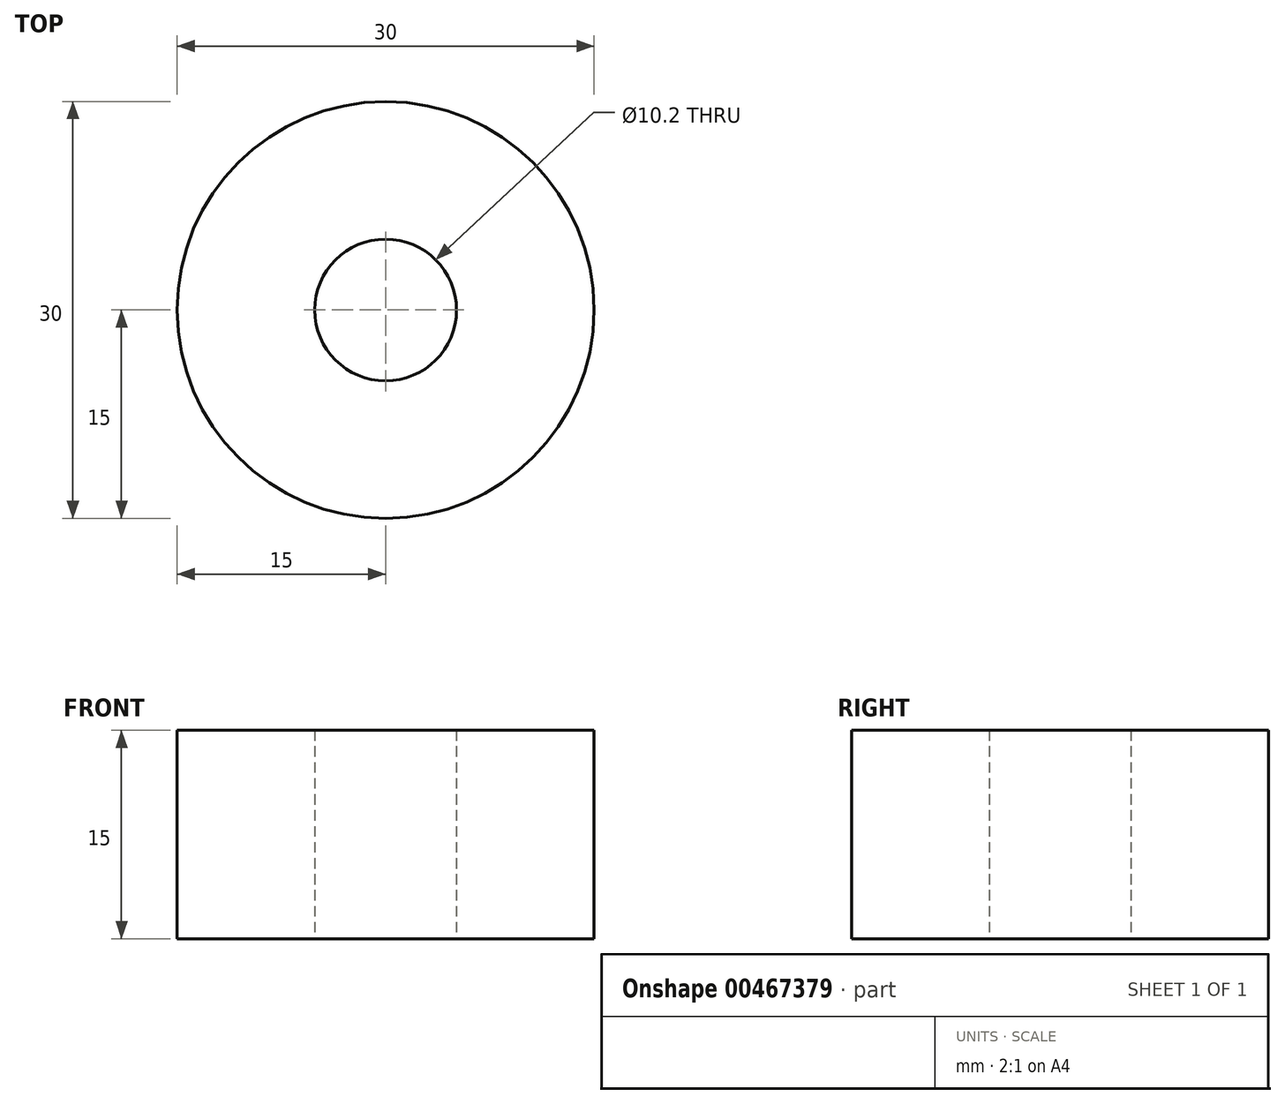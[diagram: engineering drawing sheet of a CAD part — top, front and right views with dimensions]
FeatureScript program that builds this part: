
annotation { "Feature Type Name" : "Feature", "Feature Type Description" : "" }
export const myFeature = defineFeature(function(context is Context, id is Id, definition is map)
    precondition{}
    {
        {
            var Q0;
            Q0=qCreatedBy(makeId("Top.planeOp"),FACE);
            var sketch = newSketch(context, id + "F0", { "sketchPlane" : qUnion([Q0])});
            skCircle(sketch, "E0", {"center": v(0, 0) * mm, "radius": 15 * mm});
            skCircle(sketch, "E1", {"center": v(0, 0) * mm, "radius": 5.1 * mm});
            skSolve(sketch);
        }
        {
            var Q0;
            Q0=makeQuery(id+"F0.imprint","IMPRINT",FACE,{"disambiguationData":[TD([[makeQuery(id+"F0.imprint","IMPRINT",EDGE,{"derivedFrom":sQuery(id+"F0.wireOp",EDGE,"E0")}),1.0]])]});
            extrude(context, id + "F1", {"entities" : qUnion([Q0]), "depth" : 15 * mm});
        }
    });
